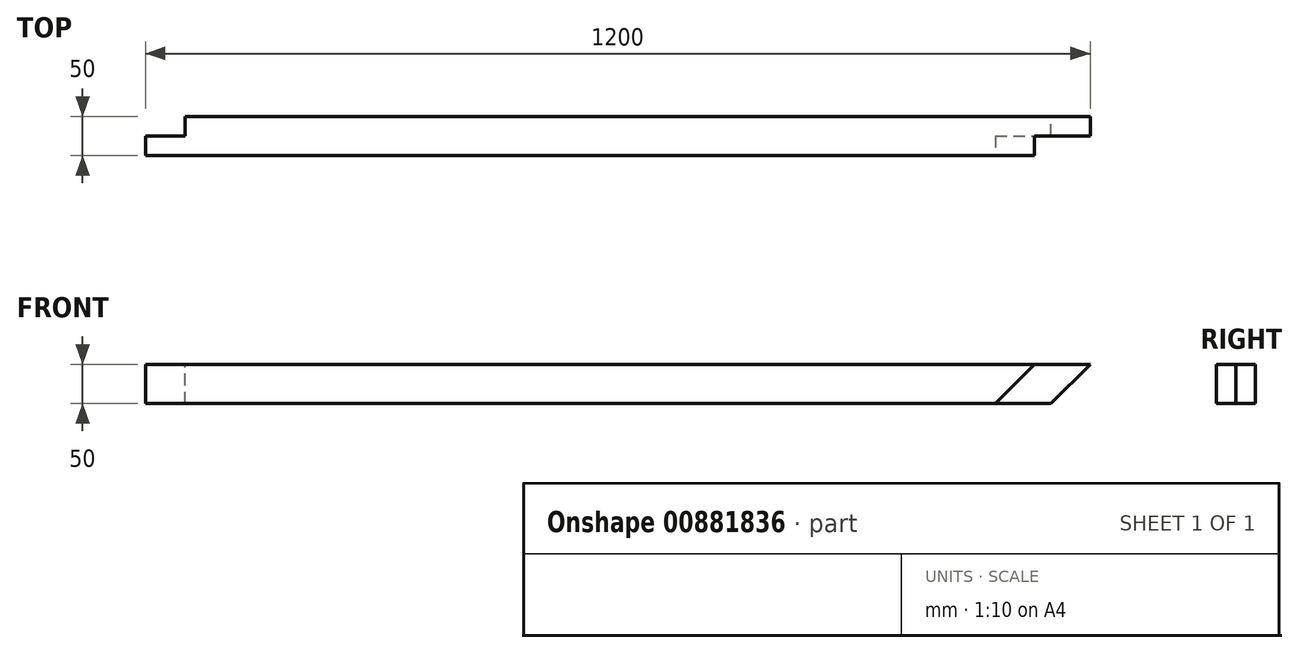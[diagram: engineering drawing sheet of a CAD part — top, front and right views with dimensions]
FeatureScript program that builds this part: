
annotation { "Feature Type Name" : "Feature", "Feature Type Description" : "" }
export const myFeature = defineFeature(function(context is Context, id is Id, definition is map)
    precondition{}
    {
        {
            var Q0;
            Q0=qCreatedBy(makeId("Front.planeOp"),FACE);
            var sketch = newSketch(context, id + "F0", { "sketchPlane" : qUnion([Q0])});
            skLineSegment(sketch, "E0", {"start": v(374.6, 24.7) * mm, "end": v(1524.6, 24.7) * mm});
            skLineSegment(sketch, "E1", {"start": v(1574.6, 74.7) * mm, "end": v(374.6, 74.7) * mm});
            skLineSegment(sketch, "E2", {"start": v(374.6, 74.7) * mm, "end": v(374.6, 24.7) * mm});
            skLineSegment(sketch, "E3.MirrorCS", {"start": v(1574.6, 74.7) * mm, "end": v(1524.6, 24.7) * mm});
            skLineSegment(sketch, "E4", {"start": v(1524.6, 24.7) * mm, "end": v(1524.6, 74.7) * mm});
            skSolve(sketch);
        }
        {
            var Q0;
            Q0=qSketchRegion(id+"F0",true);
            extrude(context, id + "F1", {"entities" : qUnion([Q0]), "depth" : 50 * mm, "offsetDistance" : 25 * mm});
        }
        {
            var Q0;
            Q0=makeQuery(id+"F1.opExtrude","CAP_FACE",FACE,{"disambiguationData":[OSD([sQuery(id+"F0.wireOp",EDGE,"E0"),sQuery(id+"F0.wireOp",EDGE,"E1"),sQuery(id+"F0.wireOp",EDGE,"E2"),sQuery(id+"F0.wireOp",EDGE,"qWGTyyMm-bhzb-qU72-nkJv-J7cF5fnZBEKZ")])],"isStart":false});
            var sketch = newSketch(context, id + "F2", { "sketchPlane" : qUnion([Q0])});
            skLineSegment(sketch, "E5", {"start": v(1574.6, 74.7) * mm, "end": v(1524.6, 24.7) * mm});
            skLineSegment(sketch, "E6", {"start": v(1524.6, 24.7) * mm, "end": v(1453.89, 24.7) * mm});
            skLineSegment(sketch, "E7", {"start": v(1453.89, 24.7) * mm, "end": v(1503.89, 74.7) * mm});
            skLineSegment(sketch, "E8", {"start": v(1503.89, 74.7) * mm, "end": v(1574.6, 74.7) * mm});
            skSolve(sketch);
        }
        {
            var Q0;
            Q0=qSketchRegion(id+"F2",true);
            extrude(context, id + "F3", {"entities" : qUnion([Q0]), "operationType" : NewBodyOperationType.REMOVE, "oppositeDirection" : true, "depth" : 25 * mm, "offsetDistance" : 25 * mm});
        }
        {
            var Q0;
            Q0=makeQuery(id+"F1.opExtrude","CAP_FACE",FACE,{"disambiguationData":[OSD([sQuery(id+"F0.wireOp",EDGE,"E0"),sQuery(id+"F0.wireOp",EDGE,"E1"),sQuery(id+"F0.wireOp",EDGE,"E2"),sQuery(id+"F0.wireOp",EDGE,"qWGTyyMm-bhzb-qU72-nkJv-J7cF5fnZBEKZ")])],"isStart":true});
            var sketch = newSketch(context, id + "F4", { "sketchPlane" : qUnion([Q0])});
            skLineSegment(sketch, "E9.bottom", {"start": v(-374.6, 24.7) * mm, "end": v(-424.6, 24.7) * mm});
            skLineSegment(sketch, "E9.top", {"start": v(-374.6, 74.7) * mm, "end": v(-424.6, 74.7) * mm});
            skLineSegment(sketch, "E9.left", {"start": v(-374.6, 24.7) * mm, "end": v(-374.6, 74.7) * mm});
            skLineSegment(sketch, "E9.right", {"start": v(-424.6, 24.7) * mm, "end": v(-424.6, 74.7) * mm});
            skSolve(sketch);
        }
        {
            var Q0;
            Q0=qSketchRegion(id+"F4",true);
            extrude(context, id + "F5", {"entities" : qUnion([Q0]), "operationType" : NewBodyOperationType.REMOVE, "oppositeDirection" : true, "depth" : 25 * mm, "offsetDistance" : 25 * mm});
        }
        {
            var Q0;
            Q0 = qSketchRegion(id + "F2", true);
            extrude(context, id + "F6", {"entities" : qUnion([Q0]), "operationType" : NewBodyOperationType.REMOVE, "oppositeDirection" : true, "depth" : 25 * mm, "offsetDistance" : 25 * mm});
        }
    });
